# Revit family: 1286xxx Ascoli Single (UL)
name_source: partatom
category: Lighting Fixtures
units: mm (PartAtom-declared; Revit-internal decimal feet)

## family parameters
Always vertical = Yes
Cut with Voids When Loaded = No
Host = Wall
Light Source = No
Maintain Annotation Orientation = No
OmniClass Number = 23.80.70.00
OmniClass Title = Lighting
Part Type = Normal
Room Calculation Point = No
Round Connector Dimension = Use Diameter
Shared = No

## types (4) — shared parameters
ADA compliant = No
Dimmable = Yes
Dimming Method = Lamp Dependent
Driver Included = Not Applicable
Driver Required = No
Efficacy (lm/w) = Lamp Dependent
Electrical Class = 1
Lamp = Halogen
Light Source Fixed = No
Location / IP Rating = Dry
Main Material = Metal - Zinc
Manufacturer = Astro Lighting Ltd
Manufacturer URL - Europe and Rest of World = www.astrolighting.com
Manufacturer URL - North America = us.astrolighting.com
Power (Watts) = Lamp Dependent
Product CCT = Lamp Dependent
Product CRI = Lamp Dependent
Product Dimensions (MM) = 125x108x120
Product Location = Interior
Product Name = Ascoli Single
Product URL = https://us.astrolighting.com
Product Weight (KG) = 0.45
URL = www.astrolighting.com
zero-valued in all types: Default Elevation

## per-type parameters (varying)
| type | Main Finish | Product SKU |
| 1286037 Ascoli Single - Textured White | Textured White | 1286037 |
| 1286042 Ascoli Single - Bronze | Bronze | 1286042 |
| 1286047 Ascoli Single - Matt Nickel | Matt Nickel | 1286047 |
| 1286120 Ascoli Single - Matt Black | Matt Black | 1286120 |

## geometry (parser evidence)
native form markers: Sweep x3
no freeform markers — native parametric forms only
